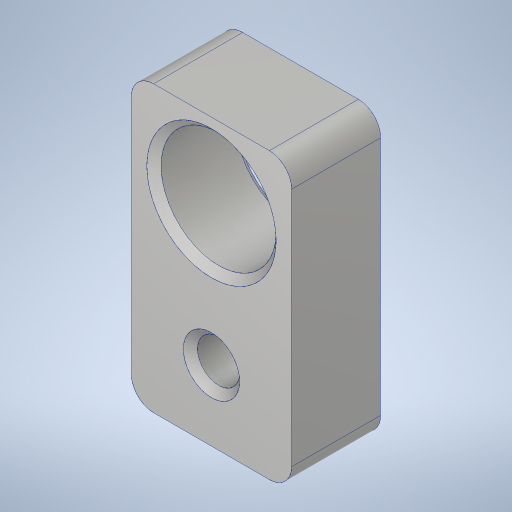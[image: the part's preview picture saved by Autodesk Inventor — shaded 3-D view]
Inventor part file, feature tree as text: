
AUTODESK INVENTOR PART (.ipt)
format: ipt  version: 2023.3 (Build 273359000, 359)  size: 262,656 bytes
history: native  units: in
note: dims shown in document units (in); Inventor stores cm internally (conversion verified against a paired STEP export)
features: sketch x3, hole x2, extrude x1, fillet x1, chamfer x1
ambient origin geometry x8: Origin, YZ Plane, XZ Plane, XY Plane, X Axis, Y Axis, Z Axis, Center Point
bodies: Solid1 (feature_tree)
feature tree (8):
  extrude  "Extrusion1"  Depth=0.45in
  hole  "Hole1"  [1 undecoded]
  hole  "Hole2"  [1 undecoded]
  fillet  "Fillet1"  Radius=0.225in
  chamfer  "Chamfer1"  Distance=0.225in
  sketch  "Sketch1"  dims[d0=0.8in d1=0.45in]
  sketch  "Sketch2"  dims[d2=0.25in d3=0.0in d5=0.197in]
  sketch  "Sketch3"  dims[d6=0.1181in d7=0.75in d8=0.332in d9=0.25in d10=0.5635in d11=1.0in d12=0.8108in d13=0.5909in d14=0.225in d15=0.3228in d16=0.75in d17=0.375in d18=0.25in d19=0.5635in d20=1.0in d21=0.8108in d22=0.225in d23=0.0625in d24=0.02in d25=0.125in d26=45.0deg]
note: 2 required parameter values undecoded (feature->parameter linkage not recoverable at this tier; creation-order binding heuristic only, values carry confidence <= 0.55)
